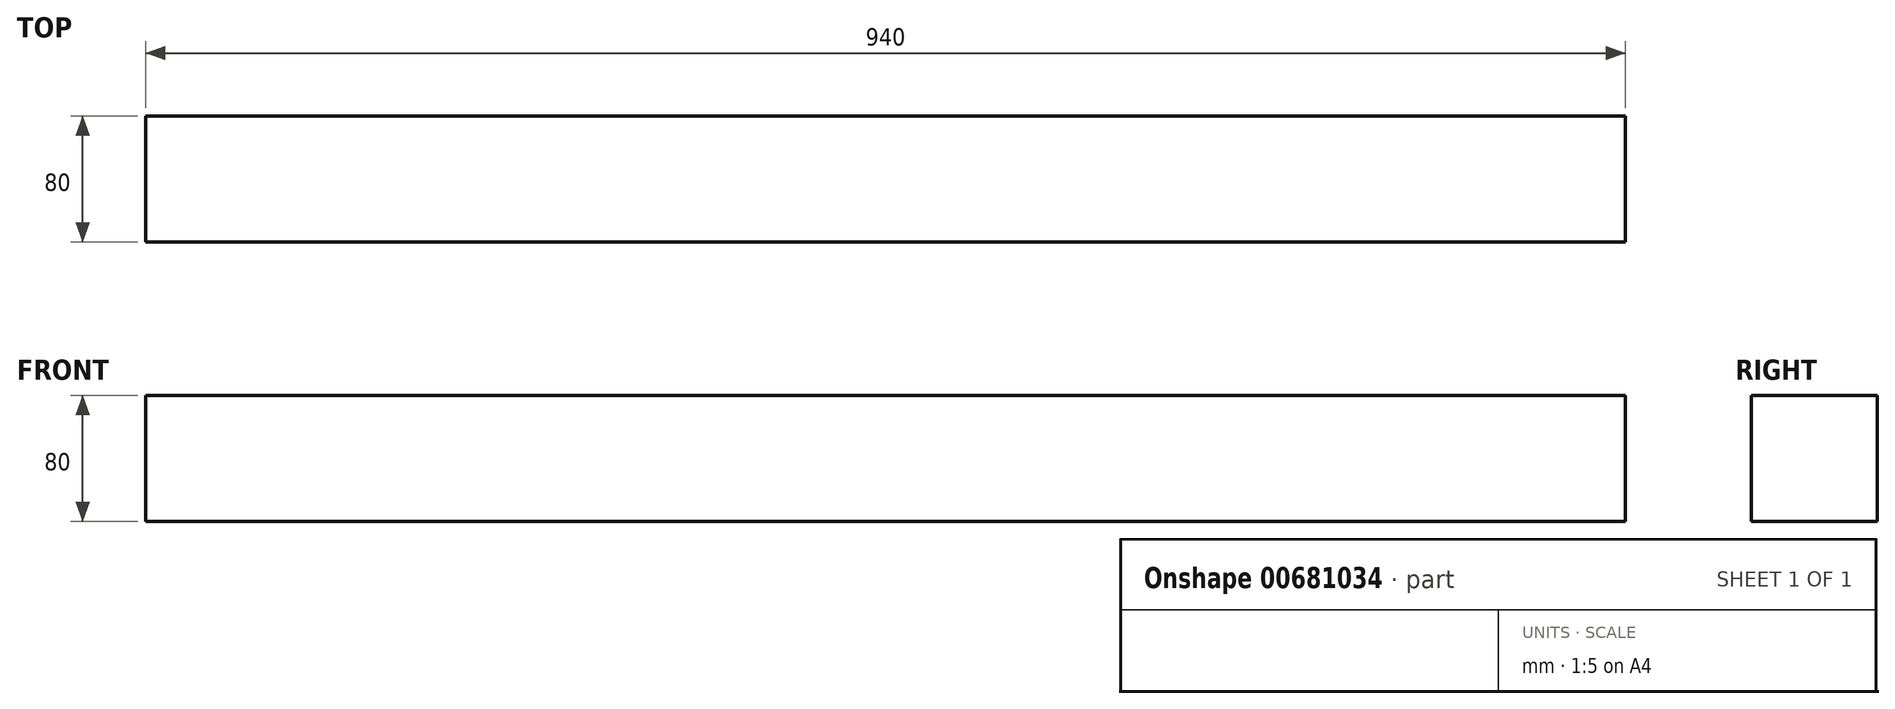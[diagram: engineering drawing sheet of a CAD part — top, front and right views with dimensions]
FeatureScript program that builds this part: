
annotation { "Feature Type Name" : "Feature", "Feature Type Description" : "" }
export const myFeature = defineFeature(function(context is Context, id is Id, definition is map)
    precondition{}
    {
        {
            var Q0;
            Q0=qCreatedBy(makeId("Front.planeOp"),FACE);
            var sketch = newSketch(context, id + "F0", { "sketchPlane" : qUnion([Q0])});
            skLineSegment(sketch, "E0.bottom", {"start": v(0, 0) * mm, "end": v(940, 0) * mm});
            skLineSegment(sketch, "E0.top", {"start": v(0, 80) * mm, "end": v(940, 80) * mm});
            skLineSegment(sketch, "E0.left", {"start": v(0, 0) * mm, "end": v(0, 80) * mm});
            skLineSegment(sketch, "E0.right", {"start": v(940, 0) * mm, "end": v(940, 80) * mm});
            skSolve(sketch);
        }
        {
            var Q0;
            Q0 = qSketchRegion(id + "F0", true);
            extrude(context, id + "F1", {"entities" : qUnion([Q0]), "depth" : 80 * mm, "offsetDistance" : 25 * mm});
        }
    });
